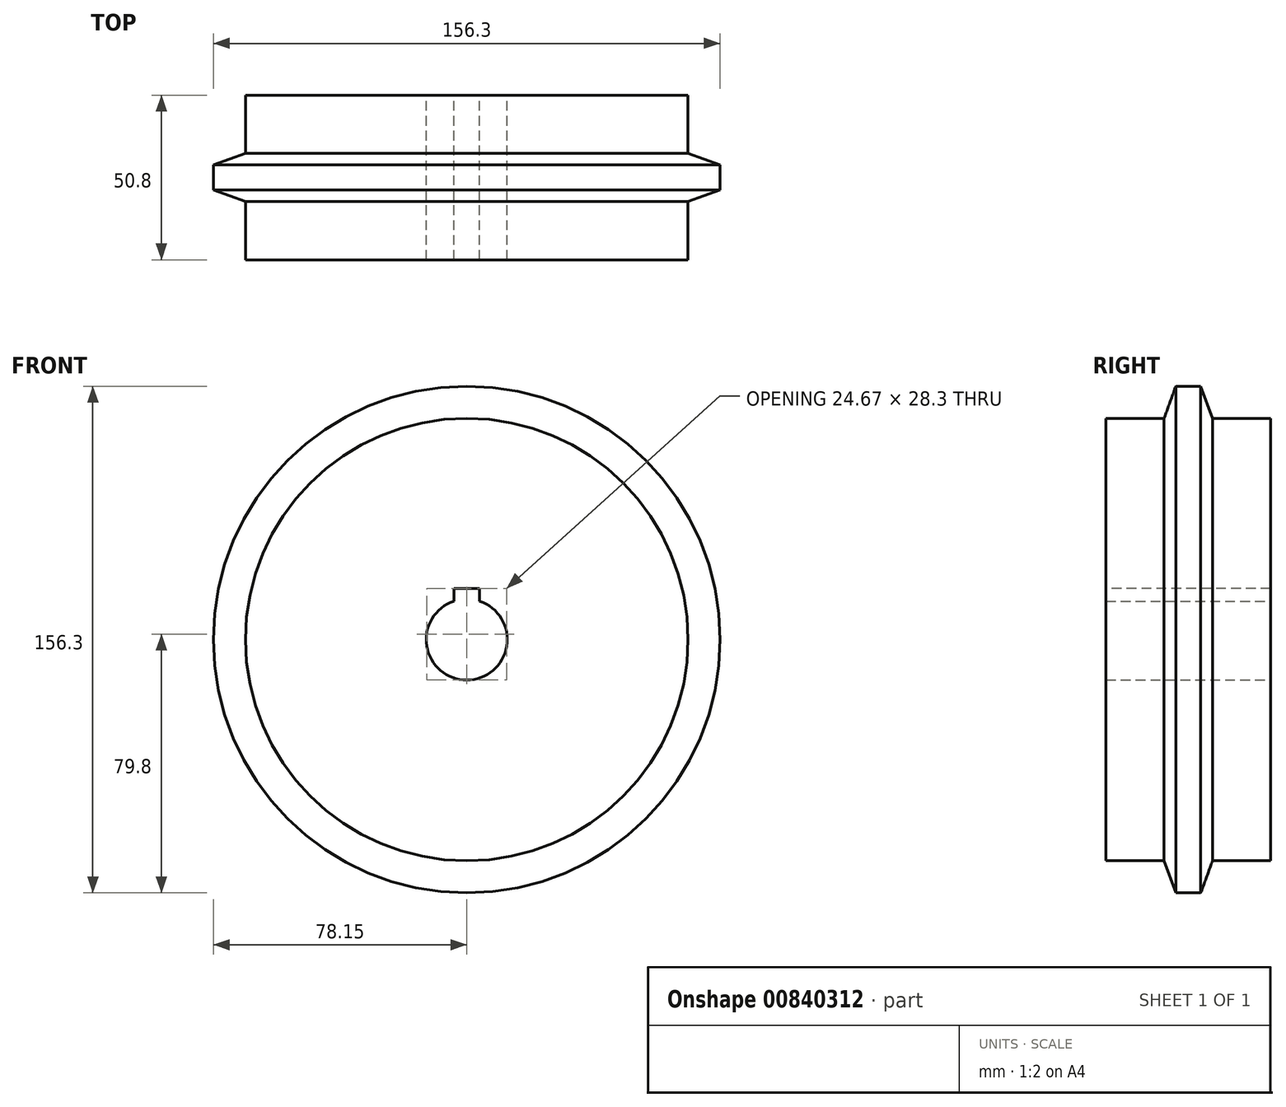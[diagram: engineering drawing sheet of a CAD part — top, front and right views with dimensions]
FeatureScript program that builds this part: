
annotation { "Feature Type Name" : "Feature", "Feature Type Description" : "" }
export const myFeature = defineFeature(function(context is Context, id is Id, definition is map)
    precondition{}
    {
        {
            var Q0;
            Q0=qCreatedBy(makeId("Front.planeOp"),FACE);
            var sketch = newSketch(context, id + "F0", { "sketchPlane" : qUnion([Q0])});
            skCircle(sketch, "E0", {"center": v(0, 0) * mm, "radius": 68.25 * mm});
            skCircle(sketch, "E1", {"center": v(0, 0) * mm, "radius": 12.5 * mm});
            skSolve(sketch);
        }
        {
            var Q0;
            Q0 = qSketchRegion(id + "F0", true);
            extrude(context, id + "F1", {"entities" : qUnion([Q0]), "endBound" : BoundingType.SYMMETRIC, "depth" : 50.8 * mm, "offsetDistance" : 25 * mm});
        }
        {
            var Q0;
            Q0=makeQuery(id+"F1.opExtrude","CAP_FACE",FACE,{"disambiguationData":[OSD([sQuery(id+"F0.wireOp",EDGE,"E0"),sQuery(id+"F0.wireOp",EDGE,"E1")])],"isStart":false});
            var sketch = newSketch(context, id + "F2", { "sketchPlane" : qUnion([Q0])});
            skLineSegment(sketch, "E2.bottom", {"start": v(-4, 0) * mm, "end": v(4, 0) * mm});
            skLineSegment(sketch, "E2.top", {"start": v(-4, 15.8) * mm, "end": v(4, 15.8) * mm});
            skLineSegment(sketch, "E2.left", {"start": v(-4, 0) * mm, "end": v(-4, 15.8) * mm});
            skLineSegment(sketch, "E2.right", {"start": v(4, 0) * mm, "end": v(4, 15.8) * mm});
            skSolve(sketch);
        }
        {
            var Q0;
            Q0 = qSketchRegion(id + "F2", true);
            extrude(context, id + "F3", {"entities" : qUnion([Q0]), "operationType" : NewBodyOperationType.REMOVE, "endBound" : BoundingType.THROUGH_ALL, "oppositeDirection" : true, "depth" : 25 * mm, "offsetDistance" : 25 * mm});
        }
        {
            var Q0;
            Q0=qCreatedBy(makeId("Front.planeOp"),FACE);
            var sketch = newSketch(context, id + "F4", { "sketchPlane" : qUnion([Q0])});
            skCircle(sketch, "E3", {"center": v(0, 0) * mm, "radius": 78.15 * mm});
            skCircle(sketch, "E4", {"center": v(0, 0) * mm, "radius": 20 * mm});
            skSolve(sketch);
        }
        {
            var Q0;
            Q0 = qSketchRegion(id + "F4", true);
            extrude(context, id + "F5", {"entities" : qUnion([Q0]), "operationType" : NewBodyOperationType.ADD, "endBound" : BoundingType.SYMMETRIC, "depth" : 15 * mm, "offsetDistance" : 25 * mm});
        }
        {
            var Q0;
            Q0=makeQuery(id+"F5.opExtrude","CAP_EDGE",EDGE,{"disambiguationData":[OSD([sQuery(id+"F4.wireOp",EDGE,"E3")])],"isStart":false});
            var Q1;
            Q1=makeQuery(id+"F5.opExtrude","CAP_EDGE",EDGE,{"disambiguationData":[OSD([sQuery(id+"F4.wireOp",EDGE,"E3")])],"isStart":true});
            chamfer(context, id + "F6", {"entities" : qUnion([Q0, Q1]), "chamferType" : ChamferType.OFFSET_ANGLE, "width" : 10 * mm, "oppositeDirection" : false, "angle" : 20 * degree, "tangentPropagation" : true});
        }
    });
